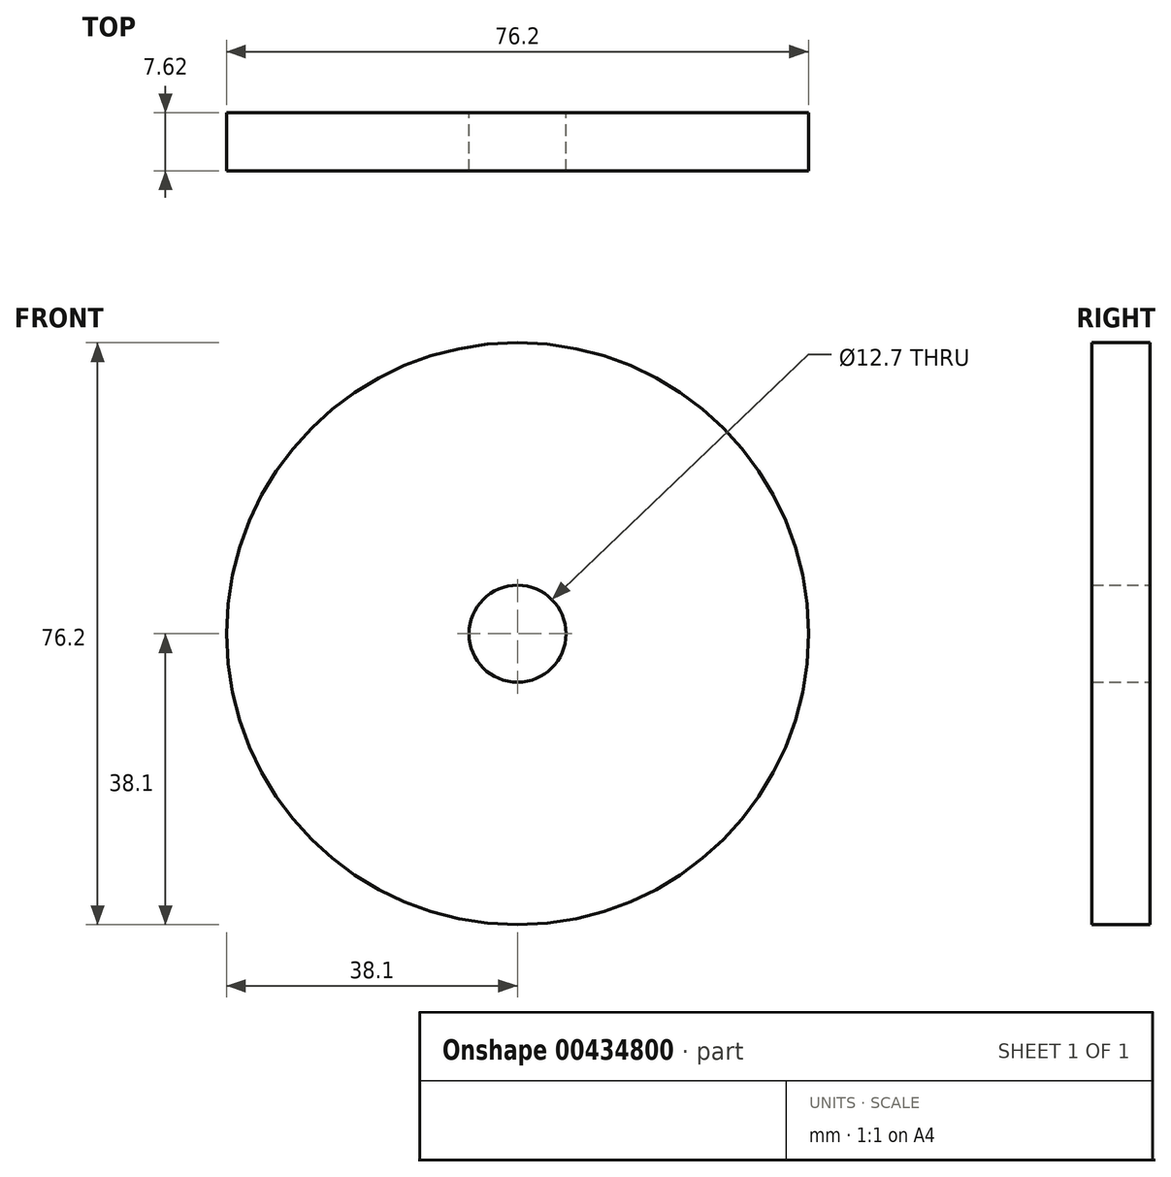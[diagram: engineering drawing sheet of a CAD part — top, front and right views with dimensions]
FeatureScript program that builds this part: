
annotation { "Feature Type Name" : "Feature", "Feature Type Description" : "" }
export const myFeature = defineFeature(function(context is Context, id is Id, definition is map)
    precondition{}
    {
        {
            var Q0;
            Q0=qCreatedBy(makeId("Front.planeOp"),FACE);
            var sketch = newSketch(context, id + "F0", { "sketchPlane" : qUnion([Q0])});
            skCircle(sketch, "E0", {"center": v(0, 0) * mm, "radius": 38.1 * mm});
            skCircle(sketch, "E1", {"center": v(0, 0) * mm, "radius": 6.35 * mm});
            skSolve(sketch);
        }
        {
            var Q0;
            Q0=makeQuery(id+"F0.imprint","IMPRINT",FACE,{"disambiguationData":[TD([[makeQuery(id+"F0.imprint","IMPRINT",EDGE,{"derivedFrom":sQuery(id+"F0.wireOp",EDGE,"E0")}),1.0]])]});
            extrude(context, id + "F1", {"entities" : qUnion([Q0]), "depth" : 7.62 * mm});
        }
    });
